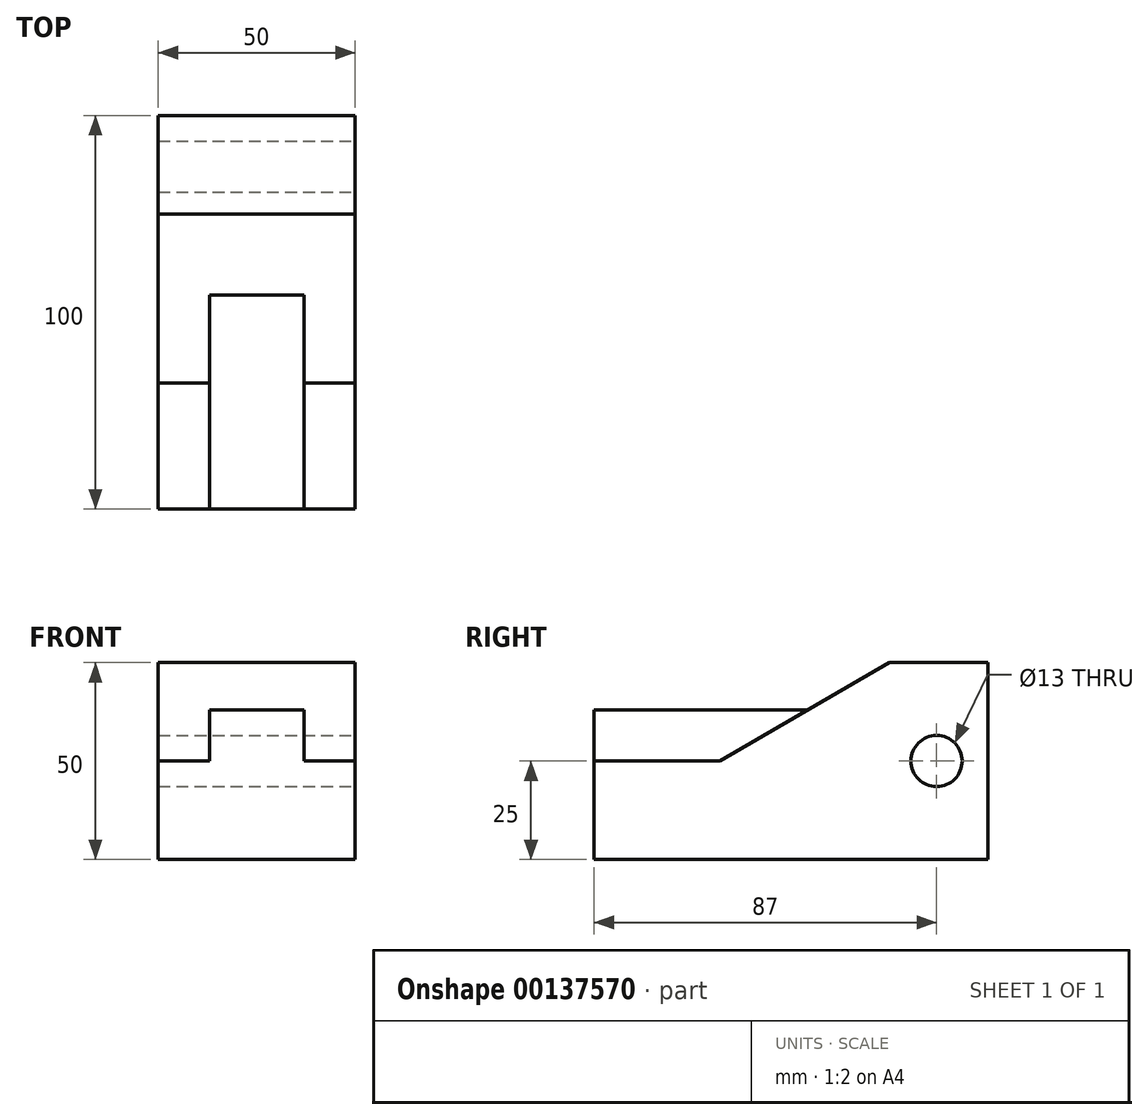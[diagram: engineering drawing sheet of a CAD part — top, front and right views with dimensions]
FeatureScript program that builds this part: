
annotation { "Feature Type Name" : "Feature", "Feature Type Description" : "" }
export const myFeature = defineFeature(function(context is Context, id is Id, definition is map)
    precondition{}
    {
        {
            var Q0;
            Q0=qCreatedBy(makeId("Right.planeOp"),FACE);
            var sketch = newSketch(context, id + "F0", { "sketchPlane" : qUnion([Q0])});
            skLineSegment(sketch, "E0", {"start": v(0, 0) * mm, "end": v(100, 0) * mm});
            skLineSegment(sketch, "E1", {"start": v(100, 0) * mm, "end": v(100, 50) * mm});
            skLineSegment(sketch, "E2", {"start": v(100, 50) * mm, "end": v(0, 50) * mm});
            skLineSegment(sketch, "E3", {"start": v(0, 50) * mm, "end": v(0, 0) * mm});
            skSolve(sketch);
        }
        {
            var Q0;
            Q0=makeQuery(id+"F0.imprint","IMPRINT",FACE,{"disambiguationData":[TD([[makeQuery(id+"F0.imprint","IMPRINT",EDGE,{"derivedFrom":sQuery(id+"F0.wireOp",EDGE,"E0")}),1.0]])]});
            extrude(context, id + "F1", {"entities" : qUnion([Q0]), "oppositeDirection" : true, "depth" : 50 * mm});
        }
        {
            var Q0;
            Q0=makeQuery(id+"F1.opExtrude","CAP_FACE",FACE,{"disambiguationData":[OSD([sQuery(id+"F0.wireOp",EDGE,"E0"),sQuery(id+"F0.wireOp",EDGE,"E1"),sQuery(id+"F0.wireOp",EDGE,"E2"),sQuery(id+"F0.wireOp",EDGE,"E3")])],"isStart":true});
            var sketch = newSketch(context, id + "F2", { "sketchPlane" : qUnion([Q0])});
            skCircle(sketch, "E4", {"center": v(87, 25) * mm, "radius": 6.5 * mm});
            skLineSegment(sketch, "E5", {"start": v(100, 50) * mm, "end": v(75, 50) * mm});
            skLineSegment(sketch, "E6", {"start": v(75, 50) * mm, "end": v(32, 25) * mm});
            skLineSegment(sketch, "E7", {"start": v(32, 25) * mm, "end": v(0, 25) * mm});
            skSolve(sketch);
        }
        {
            var Q0;
            Q0=makeQuery(id+"F2.imprint","IMPRINT",FACE,{"disambiguationData":[TD([[makeQuery(id+"F2.imprint","IMPRINT",EDGE,{"derivedFrom":sQuery(id+"F2.wireOp",EDGE,"E4")}),1.0]])]});
            extrude(context, id + "F3", {"entities" : qUnion([Q0]), "operationType" : NewBodyOperationType.REMOVE, "endBound" : BoundingType.THROUGH_ALL, "oppositeDirection" : true, "depth" : 25 * mm});
        }
        {
            var Q0;
            {var subQ0=sQuery(id+"F2.wireOp",EDGE,"E6");Q0=makeQuery(id+"F2.imprint","IMPRINT",FACE,{"disambiguationData":[TD([[makeQuery(id+"F2.imprint","IMPRINT",EDGE,{"derivedFrom":subQ0}),-1.0]])]});}
            extrude(context, id + "F4", {"entities" : qUnion([Q0]), "operationType" : NewBodyOperationType.REMOVE, "oppositeDirection" : true, "depth" : 13 * mm});
        }
        {
            var Q0;
            Q0=makeQuery(id+"F1.opExtrude","CAP_FACE",FACE,{"disambiguationData":[OSD([sQuery(id+"F0.wireOp",EDGE,"E0"),sQuery(id+"F0.wireOp",EDGE,"E1"),sQuery(id+"F0.wireOp",EDGE,"E2"),sQuery(id+"F0.wireOp",EDGE,"E3")])],"isStart":true});
            cPlane(context, id + "F5", {"entities" : qUnion([Q0]), "cplaneType" : CPlaneType.OFFSET, "offset" : 25 * mm, "oppositeDirection" : true, "width" : 150 * mm, "height" : 150 * mm});
        }
        {
            var Q0;
            Q0=makeQuery(id+"F1.opExtrude","CAP_FACE",FACE,{"disambiguationData":[OSD([sQuery(id+"F0.wireOp",EDGE,"E0"),sQuery(id+"F0.wireOp",EDGE,"E1"),sQuery(id+"F0.wireOp",EDGE,"E2"),sQuery(id+"F0.wireOp",EDGE,"E3")])],"isStart":false});
            var sketch = newSketch(context, id + "F6", { "sketchPlane" : qUnion([Q0])});
            skLineSegment(sketch, "E8", {"start": v(0, 0) * mm, "end": v(0, 25) * mm});
            skLineSegment(sketch, "E9", {"start": v(0, 25) * mm, "end": v(-32, 25) * mm});
            skLineSegment(sketch, "E10", {"start": v(-32, 25) * mm, "end": v(-75, 50) * mm});
            skLineSegment(sketch, "E11", {"start": v(-75, 50) * mm, "end": v(-100, 50) * mm});
            skSolve(sketch);
        }
        {
            var Q0;
            {var subQ0=sQuery(id+"F6.wireOp",EDGE,"E9");Q0=makeQuery(id+"F6.imprint","IMPRINT",FACE,{"disambiguationData":[TD([[makeQuery(id+"F6.imprint","IMPRINT",EDGE,{"derivedFrom":subQ0}),-1.0]])]});}
            extrude(context, id + "F7", {"entities" : qUnion([Q0]), "operationType" : NewBodyOperationType.REMOVE, "oppositeDirection" : true, "depth" : 13 * mm});
        }
        {
            var Q0;
            Q0=makeQuery(id+"F7.boolean.opBoolean","COPY",FACE,{"derivedFrom":makeQuery(id+"F7.opExtrude","CAP_FACE",FACE,{"disambiguationData":[OSD([sQuery(id+"F0.wireOp",EDGE,"E2"),sQuery(id+"F0.wireOp",EDGE,"E3"),sQuery(id+"F6.wireOp",EDGE,"E9"),sQuery(id+"F6.wireOp",EDGE,"E10")])],"isStart":false})});
            var sketch = newSketch(context, id + "F8", { "sketchPlane" : qUnion([Q0])});
            skLineSegment(sketch, "E12", {"start": v(0, 25) * mm, "end": v(0, 38) * mm});
            skLineSegment(sketch, "E13", {"start": v(0, 38) * mm, "end": v(-54.36, 38) * mm});
            skSolve(sketch);
        }
        {
            var Q0;
            {var subQ0=sQuery(id+"F8.wireOp",EDGE,"E13");Q0=makeQuery(id+"F8.imprint","IMPRINT",FACE,{"disambiguationData":[TD([[makeQuery(id+"F8.imprint","IMPRINT",EDGE,{"derivedFrom":subQ0}),-1.0]])]});}
            extrude(context, id + "F9", {"entities" : qUnion([Q0]), "operationType" : NewBodyOperationType.REMOVE, "oppositeDirection" : true, "depth" : 25 * mm});
        }
    });
